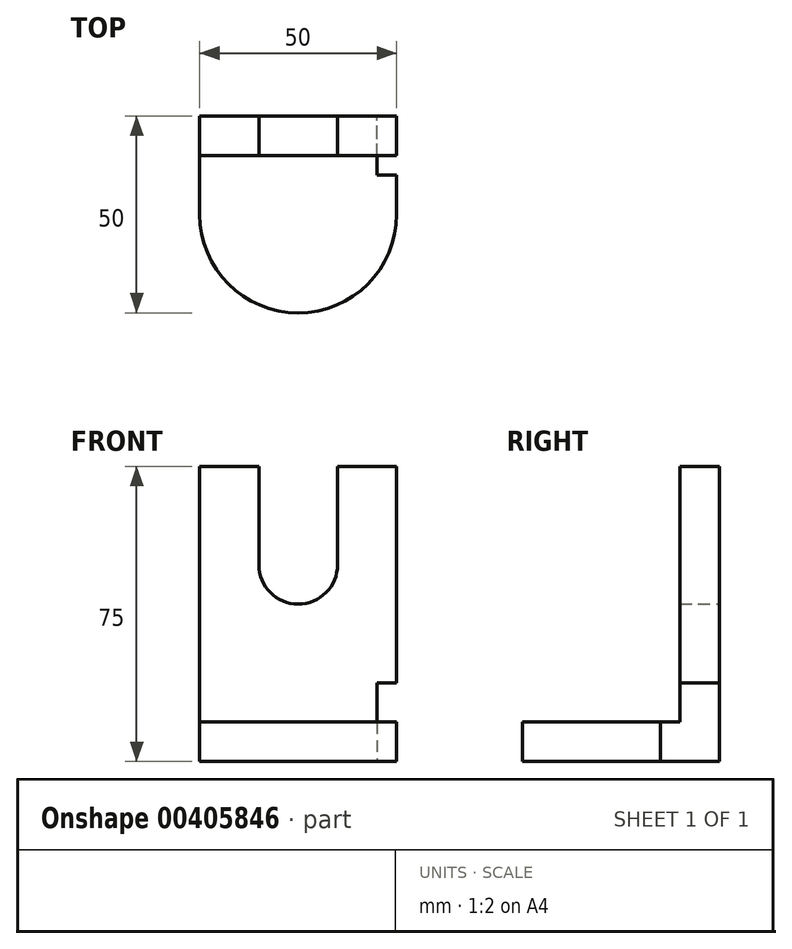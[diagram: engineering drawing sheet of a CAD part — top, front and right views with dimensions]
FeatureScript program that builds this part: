
annotation { "Feature Type Name" : "Feature", "Feature Type Description" : "" }
export const myFeature = defineFeature(function(context is Context, id is Id, definition is map)
    precondition{}
    {
        {
            var Q0;
            Q0=qCreatedBy(makeId("Front.planeOp"),FACE);
            var sketch = newSketch(context, id + "F0", { "sketchPlane" : qUnion([Q0])});
            skLineSegment(sketch, "E0.bottom", {"start": v(-25, 0) * mm, "end": v(25, 0) * mm});
            skLineSegment(sketch, "E0.top", {"start": v(-25, 75) * mm, "end": v(25, 75) * mm});
            skLineSegment(sketch, "E0.left", {"start": v(-25, 0) * mm, "end": v(-25, 75) * mm});
            skLineSegment(sketch, "E0.right", {"start": v(25, 0) * mm, "end": v(25, 75) * mm});
            skLineSegment(sketch, "E1.bottom", {"start": v(-10, 75) * mm, "end": v(10, 75) * mm});
            skLineSegment(sketch, "E1.top", {"start": v(-10, 50) * mm, "end": v(10, 50) * mm});
            skLineSegment(sketch, "E1.left", {"start": v(-10, 75) * mm, "end": v(-10, 50) * mm});
            skLineSegment(sketch, "E1.right", {"start": v(10, 75) * mm, "end": v(10, 50) * mm});
            skCircle(sketch, "E2", {"center": v(0, 50) * mm, "radius": 10 * mm});
            skPoint(sketch, "E3", {"position": v(0, 0) * mm});
            skSolve(sketch);
        }
        {
            var Q0;
            Q0=makeQuery(id+"F0.imprint","IMPRINT",FACE,{"disambiguationData":[TD([[makeQuery(id+"F0.imprint","IMPRINT",EDGE,{"derivedFrom":sQuery(id+"F0.wireOp",EDGE,"E0.bottom")}),1.0]])]});
            extrude(context, id + "F1", {"entities" : qUnion([Q0]), "depth" : 10 * mm});
        }
        {
            var Q0;
            Q0=qCreatedBy(makeId("Top.planeOp"),FACE);
            var sketch = newSketch(context, id + "F2", { "sketchPlane" : qUnion([Q0])});
            skLineSegment(sketch, "E4.0.0", {"start": v(-10, 0) * mm, "end": v(-25, 0) * mm});
            skLineSegment(sketch, "E4.0.1", {"start": v(-25, 0) * mm, "end": v(-25, -10) * mm});
            skLineSegment(sketch, "E4.0.2", {"start": v(-25, -10) * mm, "end": v(-10, -10) * mm});
            skLineSegment(sketch, "E4.0.3", {"start": v(-10, -10) * mm, "end": v(-10, 0) * mm});
            skLineSegment(sketch, "E5.0.0", {"start": v(25, 0) * mm, "end": v(10, 0) * mm});
            skLineSegment(sketch, "E5.0.1", {"start": v(10, 0) * mm, "end": v(10, -10) * mm});
            skLineSegment(sketch, "E5.0.2", {"start": v(10, -10) * mm, "end": v(25, -10) * mm});
            skLineSegment(sketch, "E5.0.3", {"start": v(25, -10) * mm, "end": v(25, 0) * mm});
            skLineSegment(sketch, "E6.0.0", {"start": v(-10, 0) * mm, "end": v(10, 0) * mm});
            skLineSegment(sketch, "E6.0.1", {"start": v(-10, 0) * mm, "end": v(-10, -10) * mm});
            skLineSegment(sketch, "E6.0.2", {"start": v(10, -10) * mm, "end": v(-10, -10) * mm});
            skLineSegment(sketch, "E6.0.3", {"start": v(10, -10) * mm, "end": v(10, 0) * mm});
            skLineSegment(sketch, "E7", {"start": v(-25, -10) * mm, "end": v(-25, -25) * mm});
            skLineSegment(sketch, "E8", {"start": v(25, -10) * mm, "end": v(25, -25) * mm});
            skArc(sketch, "E9", {"start": v(-25, -25) * mm, "mid": v(0, -50) * mm, "end": v(25, -25) * mm});
            skSolve(sketch);
        }
        {
            var Q0;
            Q0=makeQuery(id+"F2.imprint","IMPRINT",FACE,{"disambiguationData":[TD([[makeQuery(id+"F2.imprint","IMPRINT",EDGE,{"derivedFrom":sQuery(id+"F2.wireOp",EDGE,"E4.0.2")}),-1.0]])]});
            extrude(context, id + "F3", {"entities" : qUnion([Q0]), "operationType" : NewBodyOperationType.ADD, "depth" : 10 * mm});
        }
        {
            var Q0;
            Q0=makeQuery(id+"F3.boolean.opBoolean","MERGE",FACE,{"derivedFrom":[makeQuery(id+"F1.opExtrude","SWEPT_FACE",FACE,{"disambiguationData":[OSD([sQuery(id+"F0.wireOp",EDGE,"E0.right")])]}),makeQuery(id+"F3.opExtrude","SWEPT_FACE",FACE,{"disambiguationData":[OSD([sQuery(id+"F2.wireOp",EDGE,"E8")])]})]});
            var sketch = newSketch(context, id + "F4", { "sketchPlane" : qUnion([Q0])});
            skLineSegment(sketch, "E10.bottom", {"start": v(-15, 20) * mm, "end": v(15, 20) * mm});
            skLineSegment(sketch, "E10.top", {"start": v(-15, -20) * mm, "end": v(15, -20) * mm});
            skLineSegment(sketch, "E10.left", {"start": v(-15, 20) * mm, "end": v(-15, -20) * mm});
            skLineSegment(sketch, "E10.right", {"start": v(15, 20) * mm, "end": v(15, -20) * mm});
            skPoint(sketch, "E10.middle", {"position": v(0, 0) * mm});
            skSolve(sketch);
        }
        {
            var Q0;
            {var subQ0=sQuery(id+"F0.wireOp",EDGE,"E0.right");var subQ1=makeQuery(id+"F1.opExtrude","CAP_EDGE",EDGE,{"disambiguationData":[OSD([subQ0])],"isStart":false});var subQ11=sQuery(id+"F4.wireOp",EDGE,"E10.bottom");var subQ13=makeQuery(id+"F4.imprint","INTERSECT",VERTEX,{"derivedFrom":[subQ1,subQ11]});Q0=makeQuery(id+"F4.imprint","IMPRINT",FACE,{"disambiguationData":[TD([[makeQuery(id+"F4.imprint","IMPRINT",EDGE,{"disambiguationData":[TD([[subQ13,-1.0]])],"derivedFrom":subQ11}),-1.0]])]});}
            extrude(context, id + "F5", {"entities" : qUnion([Q0]), "operationType" : NewBodyOperationType.REMOVE, "oppositeDirection" : true, "depth" : 5 * mm});
        }
    });
